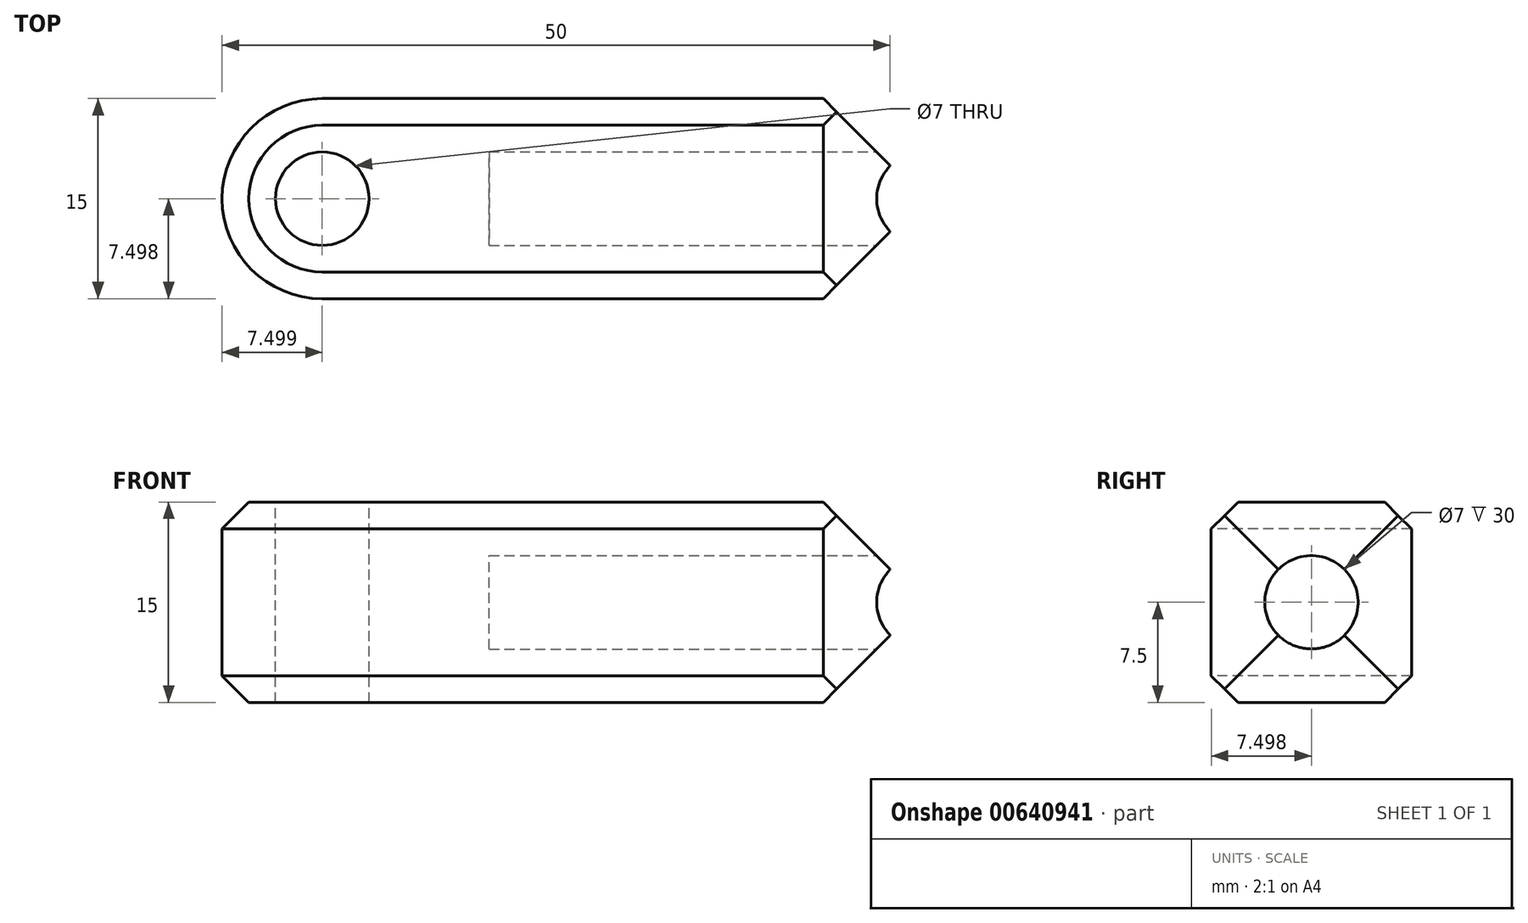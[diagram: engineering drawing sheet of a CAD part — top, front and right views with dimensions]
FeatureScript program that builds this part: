
annotation { "Feature Type Name" : "Feature", "Feature Type Description" : "" }
export const myFeature = defineFeature(function(context is Context, id is Id, definition is map)
    precondition{}
    {
        {
            var Q0;
            Q0=qCreatedBy(makeId("Top.planeOp"),FACE);
            var sketch = newSketch(context, id + "F0", { "sketchPlane" : qUnion([Q0])});
            skLineSegment(sketch, "E0.bottom", {"start": v(-59.32, 22.85) * mm, "end": v(-9.32, 22.85) * mm});
            skLineSegment(sketch, "E0.top", {"start": v(-59.32, 7.85) * mm, "end": v(-9.32, 7.85) * mm});
            skLineSegment(sketch, "E0.left", {"start": v(-59.32, 22.85) * mm, "end": v(-59.32, 7.85) * mm});
            skLineSegment(sketch, "E0.right", {"start": v(-9.32, 22.85) * mm, "end": v(-9.32, 7.85) * mm});
            skSolve(sketch);
        }
        {
            var Q0;
            Q0=makeQuery(id+"F0.imprint","IMPRINT",FACE,{"disambiguationData":[TD([[makeQuery(id+"F0.imprint","IMPRINT",EDGE,{"derivedFrom":sQuery(id+"F0.wireOp",EDGE,"E0.bottom")}),-1.0]])]});
            extrude(context, id + "F1", {"entities" : qUnion([Q0]), "depth" : 15 * mm, "offsetDistance" : 25 * mm});
        }
        {
            var Q0;
            Q0=makeQuery(id+"F1.opExtrude","SWEPT_EDGE",EDGE,{"disambiguationData":[OSD([sQuery(id+"F0.wireOp",EDGE,"E0.bottom"),sQuery(id+"F0.wireOp",EDGE,"E0.left")])]});
            var Q1;
            Q1=makeQuery(id+"F1.opExtrude","SWEPT_EDGE",EDGE,{"disambiguationData":[OSD([sQuery(id+"F0.wireOp",EDGE,"E0.top"),sQuery(id+"F0.wireOp",EDGE,"E0.left")])]});
            fillet(context, id + "F2", {"entities" : qUnion([Q0, Q1]), "radius" : 7.5 * mm, "tangentPropagation" : true, "allowEdgeOverflow" : false});
        }
        {
            var Q0;
            Q0=makeQuery(id+"F1.opExtrude","CAP_FACE",FACE,{"disambiguationData":[OSD([sQuery(id+"F0.wireOp",EDGE,"E0.bottom"),sQuery(id+"F0.wireOp",EDGE,"E0.top"),sQuery(id+"F0.wireOp",EDGE,"E0.left"),sQuery(id+"F0.wireOp",EDGE,"E0.right")])],"isStart":false});
            var sketch = newSketch(context, id + "F3", { "sketchPlane" : qUnion([Q0])});
            skCircle(sketch, "E1", {"center": v(-51.82, 15.35) * mm, "radius": 3.5 * mm});
            skSolve(sketch);
        }
        {
            var Q0;
            Q0=makeQuery(id+"F3.imprint","IMPRINT",FACE,{"disambiguationData":[TD([[makeQuery(id+"F3.imprint","IMPRINT",EDGE,{"derivedFrom":sQuery(id+"F3.wireOp",EDGE,"E1")}),1.0]])]});
            extrude(context, id + "F4", {"entities" : qUnion([Q0]), "operationType" : NewBodyOperationType.REMOVE, "oppositeDirection" : true, "depth" : 25 * mm, "offsetDistance" : 25 * mm});
        }
        {
            var Q0;
            Q0=makeQuery(id+"F1.opExtrude","SWEPT_FACE",FACE,{"disambiguationData":[OSD([sQuery(id+"F0.wireOp",EDGE,"E0.right")])]});
            var sketch = newSketch(context, id + "F5", { "sketchPlane" : qUnion([Q0])});
            skLineSegment(sketch, "E2", {"start": v(7.85, 7.5) * mm, "end": v(15.35, 7.5) * mm});
            skPoint(sketch, "E2.endSnap0", {"position": v(22.85, 7.5) * mm});
            skCircle(sketch, "E3", {"center": v(15.35, 7.5) * mm, "radius": 3.5 * mm});
            skSolve(sketch);
        }
        {
            var Q0;
            Q0=makeQuery(id+"F5.imprint","IMPRINT",FACE,{"disambiguationData":[TD([[makeQuery(id+"F5.imprint","IMPRINT",EDGE,{"derivedFrom":sQuery(id+"F5.wireOp",EDGE,"E3")}),1.0]])]});
            extrude(context, id + "F6", {"entities" : qUnion([Q0]), "operationType" : NewBodyOperationType.REMOVE, "oppositeDirection" : true, "depth" : 30 * mm, "offsetDistance" : 25 * mm});
        }
        {
            var Q0;
            Q0=makeQuery(id+"F1.opExtrude","CAP_EDGE",EDGE,{"disambiguationData":[OSD([sQuery(id+"F0.wireOp",EDGE,"E0.top")])],"isStart":false});
            var Q1;
            Q1=makeQuery(id+"F1.opExtrude","CAP_EDGE",EDGE,{"disambiguationData":[OSD([sQuery(id+"F0.wireOp",EDGE,"E0.top")])],"isStart":true});
            chamfer(context, id + "F7", {"entities" : qUnion([Q0, Q1]), "width" : 2 * mm, "tangentPropagation" : true});
        }
        {
            var Q0;
            Q0=makeQuery(id+"F1.opExtrude","CAP_EDGE",EDGE,{"disambiguationData":[OSD([sQuery(id+"F0.wireOp",EDGE,"E0.right")])],"isStart":false});
            var Q1;
            Q1=makeQuery(id+"F1.opExtrude","CAP_EDGE",EDGE,{"disambiguationData":[OSD([sQuery(id+"F0.wireOp",EDGE,"E0.right")])],"isStart":true});
            var Q2;
            Q2=makeQuery(id+"F1.opExtrude","SWEPT_EDGE",EDGE,{"disambiguationData":[OSD([sQuery(id+"F0.wireOp",EDGE,"E0.top"),sQuery(id+"F0.wireOp",EDGE,"E0.right")])]});
            var Q3;
            Q3=makeQuery(id+"F1.opExtrude","SWEPT_EDGE",EDGE,{"disambiguationData":[OSD([sQuery(id+"F0.wireOp",EDGE,"E0.bottom"),sQuery(id+"F0.wireOp",EDGE,"E0.right")])]});
            chamfer(context, id + "F8", {"entities" : qUnion([Q0, Q1, Q2, Q3]), "width" : 5 * mm, "tangentPropagation" : true});
        }
    });
